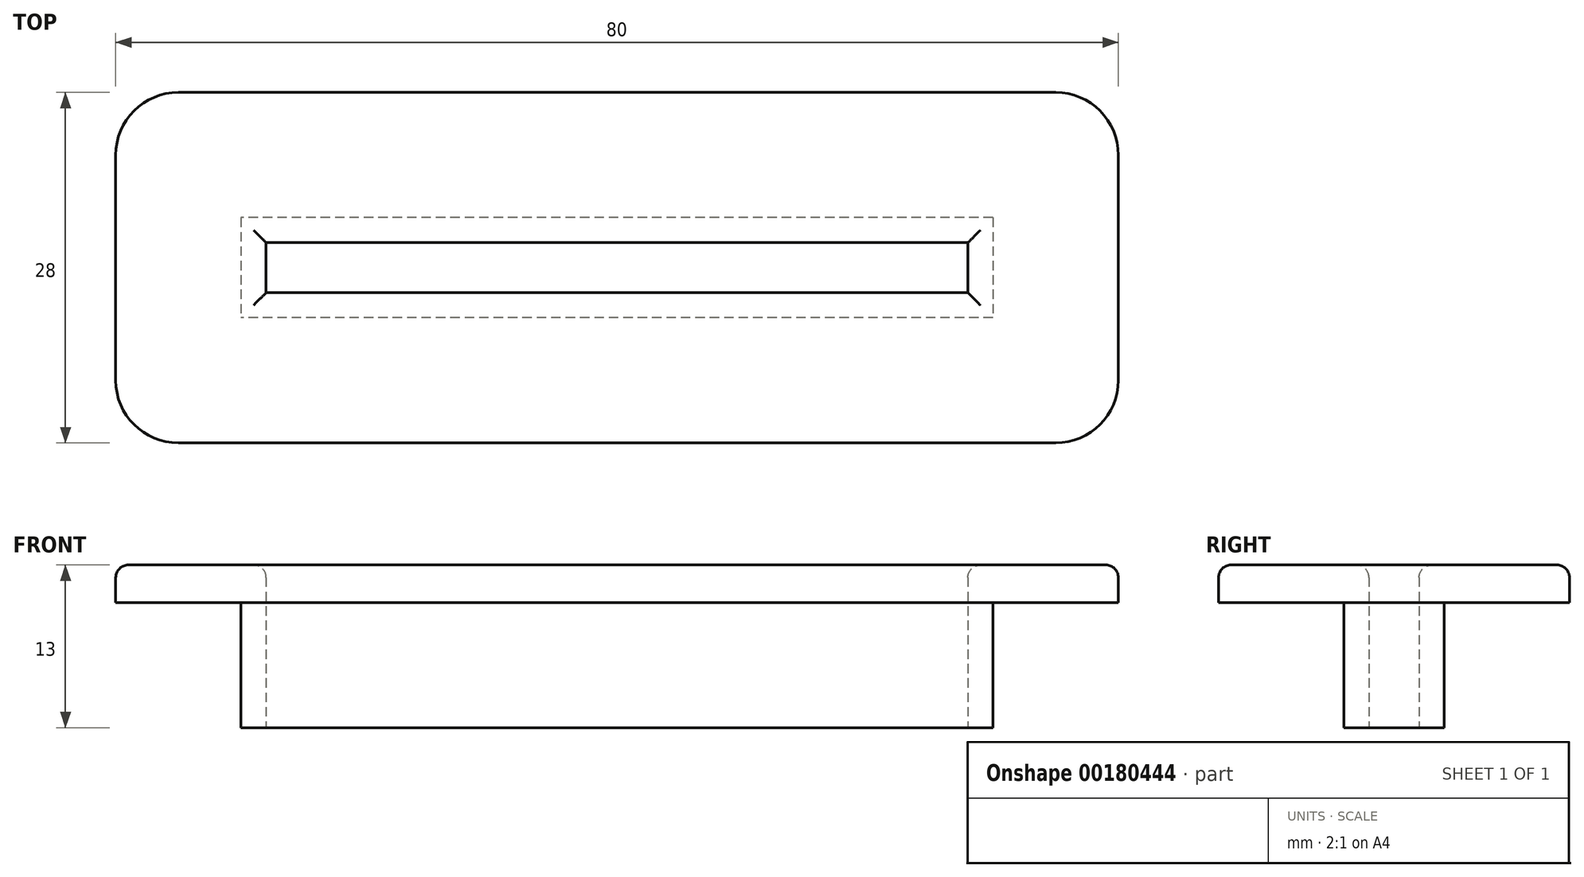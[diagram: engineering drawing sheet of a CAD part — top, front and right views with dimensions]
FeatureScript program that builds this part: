
annotation { "Feature Type Name" : "Feature", "Feature Type Description" : "" }
export const myFeature = defineFeature(function(context is Context, id is Id, definition is map)
    precondition{}
    {
        {
            var Q0;
            Q0=qCreatedBy(makeId("Top.planeOp"),FACE);
            var sketch = newSketch(context, id + "F0", { "sketchPlane" : qUnion([Q0])});
            skPoint(sketch, "E0.middle", {"position": v(0, 0) * mm});
            skLineSegment(sketch, "E1.bottom", {"start": v(40, 14) * mm, "end": v(-40, 14) * mm});
            skLineSegment(sketch, "E1.top", {"start": v(40, -14) * mm, "end": v(-40, -14) * mm});
            skLineSegment(sketch, "E1.left", {"start": v(40, 14) * mm, "end": v(40, -14) * mm});
            skLineSegment(sketch, "E1.right", {"start": v(-40, 14) * mm, "end": v(-40, -14) * mm});
            skLineSegment(sketch, "E2.bottom", {"start": v(30, 4) * mm, "end": v(-30, 4) * mm});
            skLineSegment(sketch, "E2.top", {"start": v(30, -4) * mm, "end": v(-30, -4) * mm});
            skLineSegment(sketch, "E2.left", {"start": v(30, 4) * mm, "end": v(30, -4) * mm});
            skLineSegment(sketch, "E2.right", {"start": v(-30, 4) * mm, "end": v(-30, -4) * mm});
            skLineSegment(sketch, "E3.0", {"start": v(28, 2) * mm, "end": v(-28, 2) * mm});
            skLineSegment(sketch, "E3.1", {"start": v(28, 2) * mm, "end": v(28, -2) * mm});
            skLineSegment(sketch, "E3.2", {"start": v(28, -2) * mm, "end": v(-28, -2) * mm});
            skLineSegment(sketch, "E3.3", {"start": v(-28, 2) * mm, "end": v(-28, -2) * mm});
            skLineSegment(sketch, "E4", {"start": v(30, 4) * mm, "end": v(40, 4) * mm, "construction": true});
            skLineSegment(sketch, "E5", {"start": v(30, 4) * mm, "end": v(30, 14) * mm, "construction": true});
            skSolve(sketch);
        }
        {
            var Q0;
            Q0=makeQuery(id+"F0.imprint","IMPRINT",FACE,{"disambiguationData":[TD([[makeQuery(id+"F0.imprint","IMPRINT",EDGE,{"derivedFrom":sQuery(id+"F0.wireOp",EDGE,"E2.bottom")}),1.0]])]});
            var Q1;
            Q1=makeQuery(id+"F0.imprint","IMPRINT",FACE,{"disambiguationData":[TD([[makeQuery(id+"F0.imprint","IMPRINT",EDGE,{"derivedFrom":sQuery(id+"F0.wireOp",EDGE,"E1.bottom")}),1.0]])]});
            extrude(context, id + "F1", {"entities" : qUnion([Q0, Q1]), "depth" : 3 * mm});
        }
        {
            var Q0;
            Q0=makeQuery(id+"F0.imprint","IMPRINT",FACE,{"disambiguationData":[TD([[makeQuery(id+"F0.imprint","IMPRINT",EDGE,{"derivedFrom":sQuery(id+"F0.wireOp",EDGE,"E2.bottom")}),1.0]])]});
            extrude(context, id + "F2", {"entities" : qUnion([Q0]), "operationType" : NewBodyOperationType.ADD, "oppositeDirection" : true, "depth" : 10 * mm});
        }
        {
            var Q0;
            Q0=makeQuery(id+"F1.opExtrude","SWEPT_EDGE",EDGE,{"disambiguationData":[OSD([sQuery(id+"F0.wireOp",EDGE,"E1.bottom"),sQuery(id+"F0.wireOp",EDGE,"E1.right")])]});
            var Q1;
            Q1=makeQuery(id+"F1.opExtrude","SWEPT_EDGE",EDGE,{"disambiguationData":[OSD([sQuery(id+"F0.wireOp",EDGE,"E1.top"),sQuery(id+"F0.wireOp",EDGE,"E1.right")])]});
            var Q2;
            Q2=makeQuery(id+"F1.opExtrude","SWEPT_EDGE",EDGE,{"disambiguationData":[OSD([sQuery(id+"F0.wireOp",EDGE,"E1.bottom"),sQuery(id+"F0.wireOp",EDGE,"E1.left")])]});
            var Q3;
            Q3=makeQuery(id+"F1.opExtrude","SWEPT_EDGE",EDGE,{"disambiguationData":[OSD([sQuery(id+"F0.wireOp",EDGE,"E1.top"),sQuery(id+"F0.wireOp",EDGE,"E1.left")])]});
            fillet(context, id + "F3", {"entities" : qUnion([Q0, Q1, Q2, Q3]), "radius" : 5 * mm, "tangentPropagation" : true, "allowEdgeOverflow" : false});
        }
        {
            var Q0;
            Q0=makeQuery(id+"F1.opExtrude","CAP_FACE",FACE,{"disambiguationData":[OSD([sQuery(id+"F0.wireOp",EDGE,"E1.bottom"),sQuery(id+"F0.wireOp",EDGE,"E1.top"),sQuery(id+"F0.wireOp",EDGE,"E1.left"),sQuery(id+"F0.wireOp",EDGE,"E1.right"),sQuery(id+"F0.wireOp",EDGE,"E3.0"),sQuery(id+"F0.wireOp",EDGE,"E3.1"),sQuery(id+"F0.wireOp",EDGE,"E3.2"),sQuery(id+"F0.wireOp",EDGE,"E3.3")])],"isStart":false});
            fillet(context, id + "F4", {"entities" : qUnion([Q0]), "radius" : 1 * mm, "tangentPropagation" : true, "allowEdgeOverflow" : false});
        }
    });
